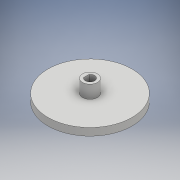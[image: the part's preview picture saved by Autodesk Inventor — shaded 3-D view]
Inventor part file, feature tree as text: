
AUTODESK INVENTOR PART (.ipt)
format: ipt  version: 2017 (Build 210142000, 142)  size: 182,784 bytes
history: native  units: mm
features: sketch x6, extrude x5, revolve x1
ambient origin geometry x8: Origin, YZ Plane, XZ Plane, XY Plane, X Axis, Y Axis, Z Axis, Center Point
bodies: Body1 (feature_tree)
feature tree (12):
  revolve  "Revolution2"  [1 undecoded]
  extrude  "Extrusion6"  Depth=7.0mm
  extrude  "Extrusion7"  Depth=4.0mm
  extrude  "Extrusion8"  Depth=4.0mm
  extrude  "Extrusion9"  Depth=4.0mm
  extrude  "Extrusion10"  Depth=4.0mm
  sketch  "Sketch1"  dims[d1=2.5mm d2=4.0mm]
  sketch  "Sketch6"  dims[d3=7.0mm d4=20.0mm]
  sketch  "Sketch7"  dims[d5=34.0mm d9=4.0mm]
  sketch  "Sketch8"  dims[d12=2.5mm d13=4.0mm]
  sketch  "Sketch9"  dims[d55=22.5mm d56=4.0mm]
  sketch  "Sketch10"  dims[d57=90.0deg d64=20.0mm d65=90.0deg d69=15.0mm d71=15.0mm d73=5.0mm d74=0.0mm d75=2.5mm d76=5.0mm d77=5.0mm d78=26.0mm d79=0.0mm d80=3.0mm d81=3.0mm d82=3.0mm d83=3.0mm d84=13.0mm d85=4.0mm d86=0.0mm d87=400.0mm d88=0.0mm d89=5.0mm d90=0.0mm]
note: 1 required parameter value undecoded (feature->parameter linkage not recoverable at this tier; creation-order binding heuristic only, values carry confidence <= 0.55)
